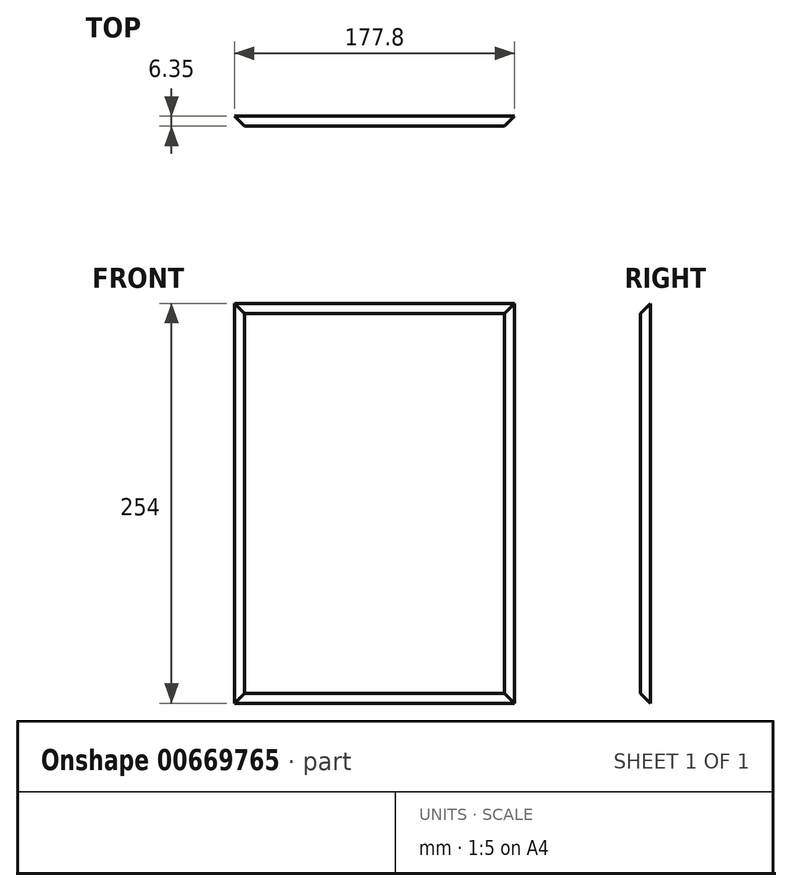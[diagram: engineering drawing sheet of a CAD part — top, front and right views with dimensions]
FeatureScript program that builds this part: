
annotation { "Feature Type Name" : "Feature", "Feature Type Description" : "" }
export const myFeature = defineFeature(function(context is Context, id is Id, definition is map)
    precondition{}
    {
        {
            var Q0;
            Q0=qCreatedBy(makeId("Front.planeOp"),FACE);
            var sketch = newSketch(context, id + "F0", { "sketchPlane" : qUnion([Q0])});
            skLineSegment(sketch, "E0.bottom", {"start": v(-150.22, 122.54) * mm, "end": v(27.58, 122.54) * mm});
            skLineSegment(sketch, "E0.top", {"start": v(-150.22, -131.46) * mm, "end": v(27.58, -131.46) * mm});
            skLineSegment(sketch, "E0.left", {"start": v(-150.22, 122.54) * mm, "end": v(-150.22, -131.46) * mm});
            skLineSegment(sketch, "E0.right", {"start": v(27.58, 122.54) * mm, "end": v(27.58, -131.46) * mm});
            skSolve(sketch);
        }
        {
            var Q0;
            Q0=makeQuery(id+"F0.imprint","IMPRINT",FACE,{"disambiguationData":[TD([[makeQuery(id+"F0.imprint","IMPRINT",EDGE,{"derivedFrom":sQuery(id+"F0.wireOp",EDGE,"E0.bottom")}),-1.0]])]});
            extrude(context, id + "F1", {"entities" : qUnion([Q0]), "depth" : 6.35 * mm, "offsetDistance" : 25.4 * mm});
        }
        {
            var Q0;
            Q0=makeQuery(id+"F1.opExtrude","CAP_FACE",FACE,{"disambiguationData":[OSD([sQuery(id+"F0.wireOp",EDGE,"E0.bottom"),sQuery(id+"F0.wireOp",EDGE,"E0.top"),sQuery(id+"F0.wireOp",EDGE,"E0.left"),sQuery(id+"F0.wireOp",EDGE,"E0.right")])],"isStart":false});
            chamfer(context, id + "F2", {"entities" : qUnion([Q0]), "chamferType" : ChamferType.OFFSET_ANGLE, "width" : 6.35 * mm, "oppositeDirection" : false, "angle" : 45 * degree, "tangentPropagation" : true});
        }
    });
